# Revit family: 432_YKA16S
name_source: partatom
category: 衛生器具
units: mm (PartAtom-declared; Revit-internal decimal feet)

## family parameters
OmniClass タイトル = Sanitary, Laundry, and Cleaning Equipment
OmniClass 番号 = 23.45.00.00
パーツ タイプ = 標準
ロード時にボイドで切り取り = はい
丸型コネクタ寸法 = 直径を使用
作業面ベース = いいえ
共有 = いいえ
常に垂直 = はい
部屋計算ポイント = いいえ

## types (1)
- YKA16S
    3Dファイル形式 = rfa
    BLCJ仕様バージョン = Version1.0
    URL = https://jp.toto.com
    キーノート = 0表示の場合は商品仕様と設計数量をご確認ください
    データ作成ソフトVer = Revit ver.2019
    モデル = YKA16S
    上水負荷単位 = 0
    中水負荷単位 = 0
    企業コード = 504860
    周波数 = 0
    商品情報URL = https://www.com-et.com
    商品紹介URL = https://jp.toto.com
    奥行 = 0
    幅 = 0
    排気配管 = はい
    排水接続口 = 0
    排水芯・排水高さ = 0  [stored 0 ft]
    排水配管 = はい
    最低使用圧力 = 0.0 MPa
    最高使用圧力 = 0.0 MPa
    極数 = 2
    構成品番 = YKA16S
    標準取付高さ = 0  [stored 0 ft]
    水配管 = はい
    汚水負荷単位 = 0
    洗浄水量 = 0.0 L
    流量（L/min） = 0
    温水配管 = はい
    相 = 1
    給水負荷単位(水栓) = 0
    給水負荷単位(洗浄) = 0
    給湯負荷単位 = 0
    製品出荷対象 = 国内
    製造元 = TOTO株式会社
    説明 = ベビーチェア コーナー設置タイプ
    負荷分類 = 9_コンセント
    雑排水負荷単位 = 0
    電圧 = 0 V

note: [stored X ft] marks values corroborated as IEEE doubles in the binary element streams (Revit-internal decimal feet)
